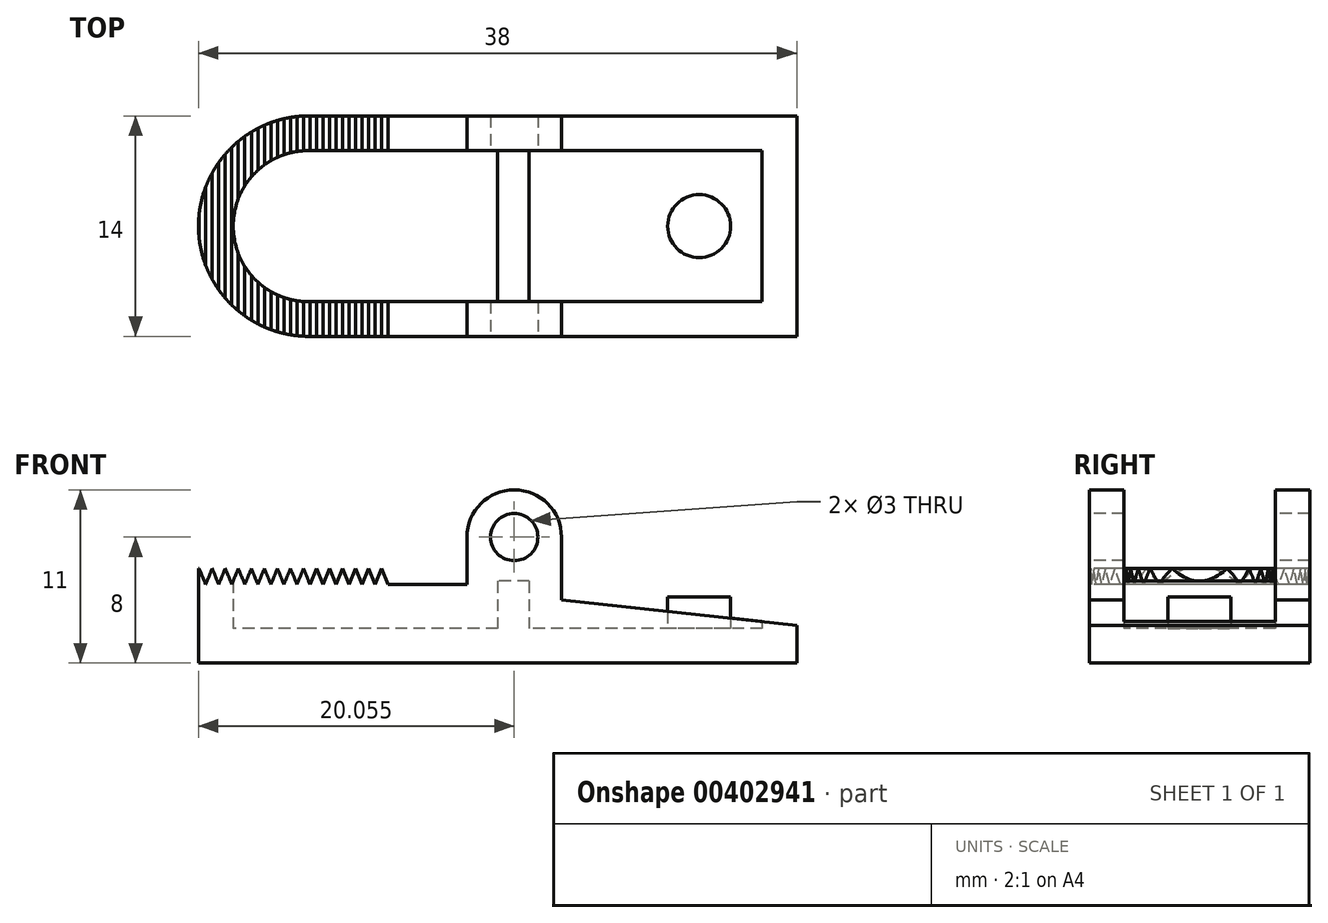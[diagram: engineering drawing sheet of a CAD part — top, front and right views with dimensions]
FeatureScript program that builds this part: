
annotation { "Feature Type Name" : "Feature", "Feature Type Description" : "" }
export const myFeature = defineFeature(function(context is Context, id is Id, definition is map)
    precondition{}
    {
        {
            var Q0;
            Q0=qCreatedBy(makeId("Top.planeOp"),FACE);
            var sketch = newSketch(context, id + "F0", { "sketchPlane" : qUnion([Q0])});
            skLineSegment(sketch, "E0", {"start": v(-12, 7) * mm, "end": v(19, 7) * mm});
            skLineSegment(sketch, "E1", {"start": v(19, 7) * mm, "end": v(19, -7) * mm});
            skLineSegment(sketch, "E2", {"start": v(19, -7) * mm, "end": v(-12, -7) * mm});
            skArc(sketch, "E3", {"start": v(-12, 7) * mm, "mid": v(-19, 0) * mm, "end": v(-12, -7) * mm});
            skSolve(sketch);
        }
        {
            var Q0;
            Q0 = qSketchRegion(id + "F0", true);
            extrude(context, id + "F1", {"entities" : qUnion([Q0]), "depth" : 25 * mm});
        }
        {
            var Q0;
            Q0=makeQuery(id+"F1.opExtrude","CAP_FACE",FACE,{"disambiguationData":[OSD([sQuery(id+"F0.wireOp",EDGE,"E0"),sQuery(id+"F0.wireOp",EDGE,"E1"),sQuery(id+"F0.wireOp",EDGE,"E2"),sQuery(id+"F0.wireOp",EDGE,"E3")])],"isStart":false});
            shell(context, id + "F2", {"entities" : qUnion([Q0]), "thickness" : 2.2 * mm});
        }
        {
            var Q0;
            Q0=qCreatedBy(makeId("Front.planeOp"),FACE);
            var sketch = newSketch(context, id + "F3", { "sketchPlane" : qUnion([Q0])});
            skLineSegment(sketch, "E4", {"start": v(4.06, 4) * mm, "end": v(4.06, 8) * mm});
            skArc(sketch, "E5", {"start": v(4.06, 8) * mm, "mid": v(1.06, 11) * mm, "end": v(-1.94, 8) * mm});
            skCircle(sketch, "E6", {"center": v(1.06, 8) * mm, "radius": 1.5 * mm});
            skLineSegment(sketch, "E7", {"start": v(-19.3, 25) * mm, "end": v(19, 25) * mm});
            skLineSegment(sketch, "E8", {"start": v(19, 25) * mm, "end": v(19, 2.4) * mm});
            skLineSegment(sketch, "E9", {"start": v(-19.3, 25) * mm, "end": v(-19.3, 6) * mm});
            skLineSegment(sketch, "E10", {"start": v(19, 2.4) * mm, "end": v(4.06, 4) * mm});
            skLineSegment(sketch, "E11", {"start": v(-19.3, 6) * mm, "end": v(-6.94, 6) * mm});
            skLineSegment(sketch, "E12", {"start": v(-6.94, 6) * mm, "end": v(-6.94, 5) * mm});
            skLineSegment(sketch, "E13", {"start": v(-6.94, 5) * mm, "end": v(-1.94, 5) * mm});
            skLineSegment(sketch, "E14", {"start": v(-1.94, 8) * mm, "end": v(-1.94, 5) * mm});
            skSolve(sketch);
        }
        {
            var Q0;
            Q0 = qSketchRegion(id + "F3", true);
            extrude(context, id + "F4", {"entities" : qUnion([Q0]), "operationType" : NewBodyOperationType.REMOVE, "endBound" : BoundingType.SYMMETRIC, "oppositeDirection" : true, "depth" : 25 * mm});
        }
        {
            var Q0;
            Q0=makeQuery(id+"F2.opShell","OFFSET_FACE",FACE,{"disambiguationData":[OSD([sQuery(id+"F0.wireOp",EDGE,"E0"),sQuery(id+"F0.wireOp",EDGE,"E1"),sQuery(id+"F0.wireOp",EDGE,"E2"),sQuery(id+"F0.wireOp",EDGE,"E3")])]});
            var sketch = newSketch(context, id + "F5", { "sketchPlane" : qUnion([Q0])});
            skCircle(sketch, "E15", {"center": v(12.8, 0) * mm, "radius": 2 * mm});
            skSolve(sketch);
        }
        {
            var Q0;
            Q0 = qSketchRegion(id + "F5", true);
            extrude(context, id + "F6", {"entities" : qUnion([Q0]), "operationType" : NewBodyOperationType.ADD, "depth" : 2 * mm});
        }
        {
            var Q0;
            Q0=makeQuery(id+"F2.opShell","OFFSET_FACE",FACE,{"disambiguationData":[OSD([sQuery(id+"F0.wireOp",EDGE,"E0"),sQuery(id+"F0.wireOp",EDGE,"E1"),sQuery(id+"F0.wireOp",EDGE,"E2"),sQuery(id+"F0.wireOp",EDGE,"E3")])]});
            var sketch = newSketch(context, id + "F7", { "sketchPlane" : qUnion([Q0])});
            skLineSegment(sketch, "E16.bottom", {"start": v(0, 4.8) * mm, "end": v(2, 4.8) * mm});
            skLineSegment(sketch, "E16.top", {"start": v(0, -4.8) * mm, "end": v(2, -4.8) * mm});
            skLineSegment(sketch, "E16.left", {"start": v(0, 4.8) * mm, "end": v(0, -4.8) * mm});
            skLineSegment(sketch, "E16.right", {"start": v(2, 4.8) * mm, "end": v(2, -4.8) * mm});
            skSolve(sketch);
        }
        {
            var Q0;
            Q0 = qSketchRegion(id + "F7", true);
            extrude(context, id + "F8", {"entities" : qUnion([Q0]), "operationType" : NewBodyOperationType.ADD, "depth" : 3 * mm});
        }
        {
            var Q0;
            Q0=makeQuery(id+"F1.opExtrude","SWEPT_FACE",FACE,{"disambiguationData":[OSD([sQuery(id+"F0.wireOp",EDGE,"E2")])]});
            var sketch = newSketch(context, id + "F9", { "sketchPlane" : qUnion([Q0])});
            skLineSegment(sketch, "E17", {"start": v(-6.53, 6) * mm, "end": v(-6.94, 5) * mm});
            skLineSegment(sketch, "E18", {"start": v(-6.94, 5) * mm, "end": v(-7.36, 6) * mm});
            skLineSegment(sketch, "E19", {"start": v(-7.36, 6) * mm, "end": v(-7.77, 5) * mm});
            skLineSegment(sketch, "E20", {"start": v(-7.77, 5) * mm, "end": v(-8.19, 6) * mm});
            skLineSegment(sketch, "E21", {"start": v(-8.19, 6) * mm, "end": v(-8.6, 5) * mm});
            skLineSegment(sketch, "E22", {"start": v(-8.6, 5) * mm, "end": v(-9.02, 6) * mm});
            skLineSegment(sketch, "E23", {"start": v(-9.02, 6) * mm, "end": v(-9.43, 5) * mm});
            skLineSegment(sketch, "E24", {"start": v(-9.43, 5) * mm, "end": v(-9.84, 6) * mm});
            skLineSegment(sketch, "E25", {"start": v(-9.84, 6) * mm, "end": v(-10.26, 5) * mm});
            skLineSegment(sketch, "E26", {"start": v(-10.26, 5) * mm, "end": v(-10.67, 6) * mm});
            skLineSegment(sketch, "E27", {"start": v(-10.67, 6) * mm, "end": v(-11.09, 5) * mm});
            skLineSegment(sketch, "E28", {"start": v(-11.09, 5) * mm, "end": v(-11.5, 6) * mm});
            skLineSegment(sketch, "E29", {"start": v(-11.5, 6) * mm, "end": v(-10.67, 6) * mm});
            skLineSegment(sketch, "E30", {"start": v(-10.67, 6) * mm, "end": v(-9.84, 6) * mm});
            skLineSegment(sketch, "E31", {"start": v(-9.84, 6) * mm, "end": v(-9.02, 6) * mm});
            skLineSegment(sketch, "E32", {"start": v(-9.02, 6) * mm, "end": v(-8.19, 6) * mm});
            skLineSegment(sketch, "E33", {"start": v(-8.19, 6) * mm, "end": v(-7.36, 6) * mm});
            skLineSegment(sketch, "E34", {"start": v(-7.36, 6) * mm, "end": v(-6.53, 6) * mm});
            skLineSegment(sketch, "E35", {"start": v(-11.5, 6) * mm, "end": v(-11.92, 5) * mm});
            skLineSegment(sketch, "E36", {"start": v(-11.92, 5) * mm, "end": v(-12.33, 6) * mm});
            skLineSegment(sketch, "E37", {"start": v(-12.33, 6) * mm, "end": v(-11.5, 6) * mm});
            skLineSegment(sketch, "E38", {"start": v(-12.33, 6) * mm, "end": v(-12.74, 5) * mm});
            skLineSegment(sketch, "E39", {"start": v(-12.74, 5) * mm, "end": v(-13.16, 6) * mm});
            skLineSegment(sketch, "E40", {"start": v(-13.16, 6) * mm, "end": v(-13.57, 5) * mm});
            skLineSegment(sketch, "E41", {"start": v(-13.57, 5) * mm, "end": v(-13.99, 6) * mm});
            skLineSegment(sketch, "E42", {"start": v(-13.99, 6) * mm, "end": v(-14.4, 5) * mm});
            skLineSegment(sketch, "E43", {"start": v(-14.4, 5) * mm, "end": v(-14.81, 6) * mm});
            skLineSegment(sketch, "E44", {"start": v(-14.81, 6) * mm, "end": v(-15.23, 5) * mm});
            skLineSegment(sketch, "E45", {"start": v(-15.23, 5) * mm, "end": v(-15.64, 6) * mm});
            skLineSegment(sketch, "E46", {"start": v(-15.64, 6) * mm, "end": v(-16.06, 5) * mm});
            skLineSegment(sketch, "E47", {"start": v(-16.06, 5) * mm, "end": v(-16.47, 6) * mm});
            skLineSegment(sketch, "E48", {"start": v(-16.47, 6) * mm, "end": v(-16.89, 5) * mm});
            skLineSegment(sketch, "E49", {"start": v(-16.89, 5) * mm, "end": v(-17.3, 6) * mm});
            skLineSegment(sketch, "E50", {"start": v(-17.3, 6) * mm, "end": v(-17.71, 5) * mm});
            skLineSegment(sketch, "E51", {"start": v(-17.71, 5) * mm, "end": v(-18.13, 6) * mm});
            skLineSegment(sketch, "E52", {"start": v(-18.13, 6) * mm, "end": v(-18.54, 5) * mm});
            skLineSegment(sketch, "E53", {"start": v(-18.54, 5) * mm, "end": v(-18.96, 6) * mm});
            skLineSegment(sketch, "E54", {"start": v(-18.96, 6) * mm, "end": v(-18.13, 6) * mm});
            skLineSegment(sketch, "E55", {"start": v(-18.13, 6) * mm, "end": v(-17.3, 6) * mm});
            skLineSegment(sketch, "E56", {"start": v(-17.3, 6) * mm, "end": v(-16.47, 6) * mm});
            skLineSegment(sketch, "E57", {"start": v(-16.47, 6) * mm, "end": v(-15.64, 6) * mm});
            skLineSegment(sketch, "E58", {"start": v(-15.64, 6) * mm, "end": v(-14.81, 6) * mm});
            skLineSegment(sketch, "E59", {"start": v(-14.81, 6) * mm, "end": v(-13.99, 6) * mm});
            skLineSegment(sketch, "E60", {"start": v(-13.99, 6) * mm, "end": v(-13.16, 6) * mm});
            skLineSegment(sketch, "E61", {"start": v(-13.16, 6) * mm, "end": v(-12.33, 6) * mm});
            skSolve(sketch);
        }
        {
            var Q0;
            Q0 = qSketchRegion(id + "F9", true);
            var Q1;
            Q1=makeQuery(id+"F1.opExtrude","SWEPT_FACE",FACE,{"disambiguationData":[OSD([sQuery(id+"F0.wireOp",EDGE,"E0")])]});
            extrude(context, id + "F10", {"entities" : qUnion([Q0]), "operationType" : NewBodyOperationType.REMOVE, "endBound" : BoundingType.UP_TO_SURFACE, "oppositeDirection" : true, "endBoundEntityFace" : qUnion([Q1]), "depth" : 14 * mm});
        }
    });
